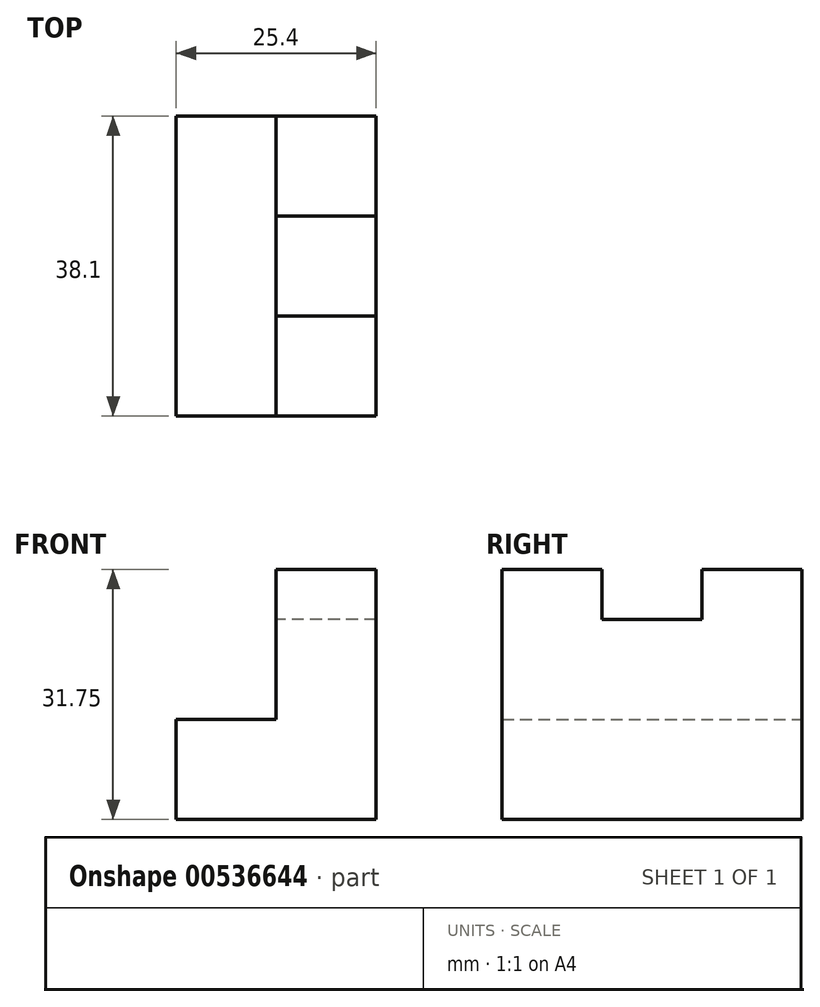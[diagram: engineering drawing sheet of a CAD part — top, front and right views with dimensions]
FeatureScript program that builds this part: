
annotation { "Feature Type Name" : "Feature", "Feature Type Description" : "" }
export const myFeature = defineFeature(function(context is Context, id is Id, definition is map)
    precondition{}
    {
        {
            var Q0;
            Q0=qCreatedBy(makeId("Front.planeOp"),FACE);
            var sketch = newSketch(context, id + "F0", { "sketchPlane" : qUnion([Q0])});
            skLineSegment(sketch, "E0", {"start": v(-19.92, 47.74) * mm, "end": v(-19.92, 15.99) * mm});
            skLineSegment(sketch, "E1", {"start": v(-19.92, 15.99) * mm, "end": v(-45.32, 15.99) * mm});
            skLineSegment(sketch, "E2", {"start": v(-45.32, 15.99) * mm, "end": v(-45.32, 28.69) * mm});
            skLineSegment(sketch, "E3", {"start": v(-45.32, 28.69) * mm, "end": v(-32.62, 28.69) * mm});
            skLineSegment(sketch, "E4", {"start": v(-19.92, 47.74) * mm, "end": v(-32.62, 47.74) * mm});
            skLineSegment(sketch, "E5", {"start": v(-32.62, 47.74) * mm, "end": v(-32.62, 28.69) * mm});
            skSolve(sketch);
        }
        {
            var Q0;
            Q0 = qSketchRegion(id + "F0", true);
            extrude(context, id + "F1", {"entities" : qUnion([Q0]), "depth" : 38.1 * mm, "offsetDistance" : 25.4 * mm});
        }
        {
            var Q0;
            Q0=makeQuery(id+"F1.opExtrude","SWEPT_FACE",FACE,{"disambiguationData":[OSD([sQuery(id+"F0.wireOp",EDGE,"E5")])]});
            var sketch = newSketch(context, id + "F2", { "sketchPlane" : qUnion([Q0])});
            skLineSegment(sketch, "E6", {"start": v(12.7, 47.74) * mm, "end": v(12.7, 41.39) * mm});
            skLineSegment(sketch, "E7", {"start": v(12.7, 41.39) * mm, "end": v(25.4, 41.39) * mm});
            skLineSegment(sketch, "E8", {"start": v(25.4, 41.39) * mm, "end": v(25.4, 47.74) * mm});
            skSolve(sketch);
        }
        {
            var Q0;
            {var subQ0=sQuery(id+"F2.wireOp",EDGE,"E6");Q0=makeQuery(id+"F2.imprint","IMPRINT",FACE,{"disambiguationData":[TD([[makeQuery(id+"F2.imprint","IMPRINT",EDGE,{"derivedFrom":subQ0}),1.0]])]});}
            extrude(context, id + "F3", {"entities" : qUnion([Q0]), "operationType" : NewBodyOperationType.REMOVE, "endBound" : BoundingType.THROUGH_ALL, "oppositeDirection" : true, "depth" : 25.4 * mm, "offsetDistance" : 25.4 * mm});
        }
    });
